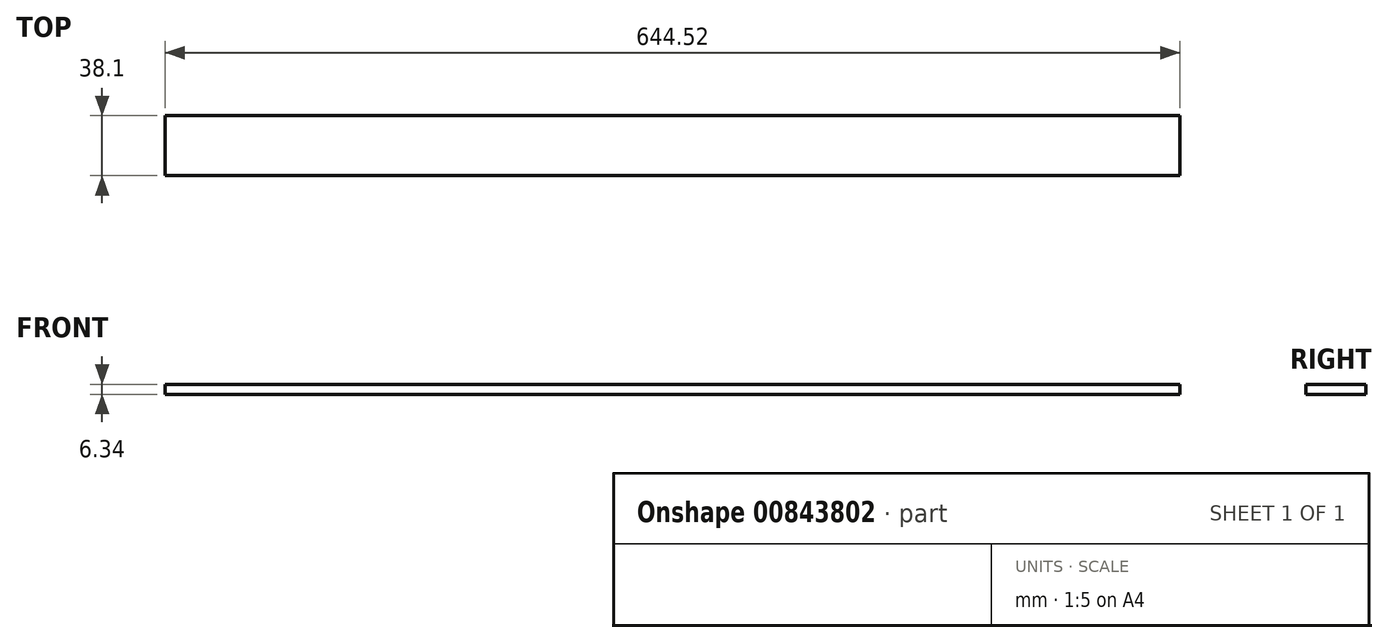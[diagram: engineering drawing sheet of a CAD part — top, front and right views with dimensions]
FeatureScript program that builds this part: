
annotation { "Feature Type Name" : "Feature", "Feature Type Description" : "" }
export const myFeature = defineFeature(function(context is Context, id is Id, definition is map)
    precondition{}
    {
        {
            var Q0;
            Q0=qCreatedBy(makeId("Front.planeOp"),FACE);
            var sketch = newSketch(context, id + "F0", { "sketchPlane" : qUnion([Q0])});
            skLineSegment(sketch, "E0.bottom", {"start": v(322.26, 3.18) * mm, "end": v(-322.26, 3.18) * mm});
            skLineSegment(sketch, "E0.top", {"start": v(322.26, -3.18) * mm, "end": v(-322.26, -3.18) * mm});
            skLineSegment(sketch, "E0.left", {"start": v(322.26, 3.18) * mm, "end": v(322.26, -3.18) * mm});
            skLineSegment(sketch, "E0.right", {"start": v(-322.26, 3.18) * mm, "end": v(-322.26, -3.18) * mm});
            skPoint(sketch, "E0.middle", {"position": v(0, 0) * mm});
            skSolve(sketch);
        }
        {
            var Q0;
            Q0 = qSketchRegion(id + "F0", true);
            extrude(context, id + "F1", {"entities" : qUnion([Q0]), "depth" : 38.1 * mm, "offsetDistance" : 25.4 * mm});
        }
    });
